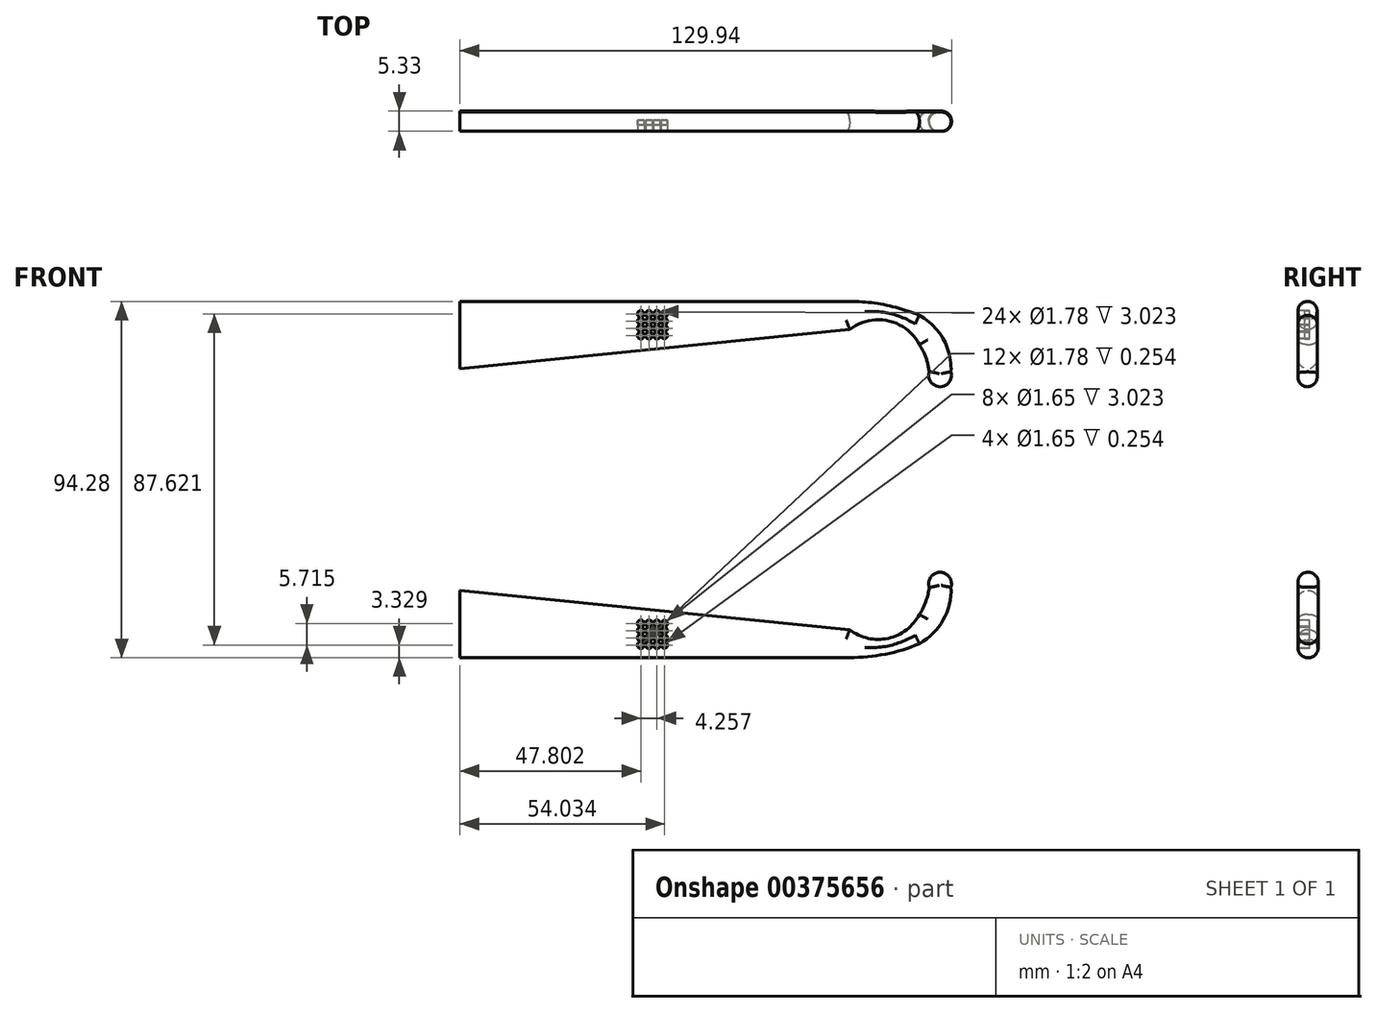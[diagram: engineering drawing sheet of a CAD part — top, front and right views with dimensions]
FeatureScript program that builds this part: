
annotation { "Feature Type Name" : "Feature", "Feature Type Description" : "" }
export const myFeature = defineFeature(function(context is Context, id is Id, definition is map)
    precondition{}
    {
        {
            var Q0;
            Q0=qCreatedBy(makeId("Front.planeOp"),FACE);
            var sketch = newSketch(context, id + "F0", { "sketchPlane" : qUnion([Q0])});
            skLineSegment(sketch, "E0", {"start": v(-73.1, 47.14) * mm, "end": v(-73.1, 29.36) * mm});
            skLineSegment(sketch, "E1", {"start": v(-73.1, 47.14) * mm, "end": v(29.93, 47.14) * mm});
            skLineSegment(sketch, "E2", {"start": v(-73.1, 29.36) * mm, "end": v(29.93, 39.72) * mm});
            skArc(sketch, "E3", {"start": v(48.35, 43.46) * mm, "mid": v(39.32, 46.2) * mm, "end": v(29.93, 47.14) * mm});
            skArc(sketch, "E4", {"start": v(56.7, 28.5) * mm, "mid": v(54.65, 37.16) * mm, "end": v(48.35, 43.46) * mm});
            skArc(sketch, "E5", {"start": v(48.35, 35.69) * mm, "mid": v(40.09, 42.02) * mm, "end": v(29.93, 39.72) * mm});
            skArc(sketch, "E6", {"start": v(50.94, 28.5) * mm, "mid": v(50.07, 32.24) * mm, "end": v(48.35, 35.69) * mm});
            skArc(sketch, "E7", {"start": v(50.94, 28.5) * mm, "mid": v(53.82, 24.55) * mm, "end": v(56.7, 28.5) * mm});
            skLineSegment(sketch, "E8", {"start": v(-76.71, 0) * mm, "end": v(75.51, 0) * mm});
            skLineSegment(sketch, "E9.MirrorCS", {"start": v(-73.1, -29.36) * mm, "end": v(29.93, -39.72) * mm});
            skLineSegment(sketch, "E10.MirrorCS", {"start": v(-73.1, -47.14) * mm, "end": v(29.93, -47.14) * mm});
            skLineSegment(sketch, "E11.MirrorCS", {"start": v(-73.1, -47.14) * mm, "end": v(-73.1, -29.36) * mm});
            skArc(sketch, "E12.MirrorCS", {"start": v(48.35, -43.46) * mm, "mid": v(39.32, -46.2) * mm, "end": v(29.93, -47.14) * mm});
            skArc(sketch, "E13.MirrorCS", {"start": v(56.7, -28.5) * mm, "mid": v(54.65, -37.16) * mm, "end": v(48.35, -43.46) * mm});
            skArc(sketch, "E14.MirrorCS", {"start": v(50.94, -28.5) * mm, "mid": v(53.82, -24.55) * mm, "end": v(56.7, -28.5) * mm});
            skArc(sketch, "E15.MirrorCS", {"start": v(50.94, -28.5) * mm, "mid": v(50.07, -32.24) * mm, "end": v(48.35, -35.69) * mm});
            skArc(sketch, "E16.MirrorCS", {"start": v(48.35, -35.69) * mm, "mid": v(40.09, -42.02) * mm, "end": v(29.93, -39.72) * mm});
            skSolve(sketch);
        }
        {
            var Q0;
            Q0 = qSketchRegion(id + "F0", true);
            extrude(context, id + "F1", {"entities" : qUnion([Q0]), "depth" : 5.08 * mm});
        }
        {
            var Q0;
            Q0=makeQuery(id+"F1.opExtrude","CAP_EDGE",EDGE,{"disambiguationData":[OSD([sQuery(id+"F0.wireOp",EDGE,"E3")])],"isStart":false});
            var Q1;
            Q1=makeQuery(id+"F1.opExtrude","CAP_EDGE",EDGE,{"disambiguationData":[OSD([sQuery(id+"F0.wireOp",EDGE,"E3")])],"isStart":true});
            var Q2;
            Q2=makeQuery(id+"F1.opExtrude","CAP_EDGE",EDGE,{"disambiguationData":[OSD([sQuery(id+"F0.wireOp",EDGE,"E4")])],"isStart":false});
            var Q3;
            Q3=makeQuery(id+"F1.opExtrude","CAP_EDGE",EDGE,{"disambiguationData":[OSD([sQuery(id+"F0.wireOp",EDGE,"E6")])],"isStart":false});
            var Q4;
            Q4=makeQuery(id+"F1.opExtrude","CAP_EDGE",EDGE,{"disambiguationData":[OSD([sQuery(id+"F0.wireOp",EDGE,"E5")])],"isStart":false});
            var Q5;
            Q5=makeQuery(id+"F1.opExtrude","CAP_EDGE",EDGE,{"disambiguationData":[OSD([sQuery(id+"F0.wireOp",EDGE,"E7")])],"isStart":false});
            var Q6;
            Q6=makeQuery(id+"F1.opExtrude","CAP_EDGE",EDGE,{"disambiguationData":[OSD([sQuery(id+"F0.wireOp",EDGE,"E7")])],"isStart":true});
            var Q7;
            Q7=makeQuery(id+"F1.opExtrude","CAP_EDGE",EDGE,{"disambiguationData":[OSD([sQuery(id+"F0.wireOp",EDGE,"E4")])],"isStart":true});
            var Q8;
            Q8=makeQuery(id+"F1.opExtrude","CAP_EDGE",EDGE,{"disambiguationData":[OSD([sQuery(id+"F0.wireOp",EDGE,"E6")])],"isStart":true});
            var Q9;
            Q9=makeQuery(id+"F1.opExtrude","CAP_EDGE",EDGE,{"disambiguationData":[OSD([sQuery(id+"F0.wireOp",EDGE,"E5")])],"isStart":true});
            var Q10;
            Q10=makeQuery(id+"F1.opExtrude","CAP_EDGE",EDGE,{"disambiguationData":[OSD([sQuery(id+"F0.wireOp",EDGE,"E2")])],"isStart":false});
            var Q11;
            Q11=makeQuery(id+"F1.opExtrude","CAP_EDGE",EDGE,{"disambiguationData":[OSD([sQuery(id+"F0.wireOp",EDGE,"E2")])],"isStart":true});
            fillet(context, id + "F2", {"entities" : qUnion([Q0, Q1, Q2, Q3, Q4, Q5, Q6, Q7, Q8, Q9, Q10, Q11]), "radius" : 2.54 * mm, "tangentPropagation" : true, "allowEdgeOverflow" : false});
        }
        {
            var Q0;
            Q0=makeQuery(id+"F2.opFillet","SPLIT",FACE,{"disambiguationData":[OD(0.0)],"derivedFrom":makeQuery(id+"F1.opExtrude","CAP_FACE",FACE,{"disambiguationData":[OSD([sQuery(id+"F0.wireOp",EDGE,"E0"),sQuery(id+"F0.wireOp",EDGE,"E1"),sQuery(id+"F0.wireOp",EDGE,"E2"),sQuery(id+"F0.wireOp",EDGE,"E3"),sQuery(id+"F0.wireOp",EDGE,"E4"),sQuery(id+"F0.wireOp",EDGE,"E5"),sQuery(id+"F0.wireOp",EDGE,"E6"),sQuery(id+"F0.wireOp",EDGE,"E7")])],"isStart":false})});
            var sketch = newSketch(context, id + "F3", { "sketchPlane" : qUnion([Q0])});
            skCircle(sketch, "E17", {"center": v(-21.04, 43.81) * mm, "radius": 0.89 * mm});
            skCircle(sketch, "E18", {"center": v(-21.05, 41.9) * mm, "radius": 0.89 * mm});
            skCircle(sketch, "E19", {"center": v(-21.05, 40) * mm, "radius": 0.89 * mm});
            skCircle(sketch, "E20", {"center": v(-21.05, 38.1) * mm, "radius": 0.89 * mm});
            skCircle(sketch, "E21", {"center": v(-19.07, 43.81) * mm, "radius": 0.83 * mm});
            skCircle(sketch, "E22", {"center": v(-19.07, 41.89) * mm, "radius": 0.83 * mm});
            skCircle(sketch, "E23", {"center": v(-19.07, 40) * mm, "radius": 0.83 * mm});
            skCircle(sketch, "E24", {"center": v(-19.07, 38.1) * mm, "radius": 0.83 * mm});
            skCircle(sketch, "E25", {"center": v(-23.16, 43.81) * mm, "radius": 0.89 * mm});
            skCircle(sketch, "E26", {"center": v(-23.16, 41.89) * mm, "radius": 0.89 * mm});
            skCircle(sketch, "E27", {"center": v(-23.16, 40) * mm, "radius": 0.89 * mm});
            skCircle(sketch, "E28", {"center": v(-23.16, 38.1) * mm, "radius": 0.89 * mm});
            skCircle(sketch, "E29", {"center": v(-25.3, 43.81) * mm, "radius": 0.89 * mm});
            skCircle(sketch, "E30", {"center": v(-25.3, 41.89) * mm, "radius": 0.89 * mm});
            skCircle(sketch, "E31", {"center": v(-25.3, 40) * mm, "radius": 0.89 * mm});
            skCircle(sketch, "E32", {"center": v(-25.3, 38.1) * mm, "radius": 0.89 * mm});
            skCircle(sketch, "E33.MirrorC", {"center": v(-19.07, -43.81) * mm, "radius": 0.83 * mm});
            skCircle(sketch, "E34.MirrorC", {"center": v(-21.04, -43.81) * mm, "radius": 0.89 * mm});
            skCircle(sketch, "E35.MirrorC", {"center": v(-23.16, -43.81) * mm, "radius": 0.89 * mm});
            skCircle(sketch, "E36.MirrorC", {"center": v(-25.3, -43.81) * mm, "radius": 0.89 * mm});
            skCircle(sketch, "E37.MirrorC", {"center": v(-19.07, -41.89) * mm, "radius": 0.83 * mm});
            skCircle(sketch, "E38.MirrorC", {"center": v(-21.05, -41.9) * mm, "radius": 0.89 * mm});
            skCircle(sketch, "E39.MirrorC", {"center": v(-23.16, -41.89) * mm, "radius": 0.89 * mm});
            skCircle(sketch, "E40.MirrorC", {"center": v(-25.3, -41.89) * mm, "radius": 0.89 * mm});
            skCircle(sketch, "E41.MirrorC", {"center": v(-19.07, -40) * mm, "radius": 0.83 * mm});
            skCircle(sketch, "E42.MirrorC", {"center": v(-21.05, -40) * mm, "radius": 0.89 * mm});
            skCircle(sketch, "E43.MirrorC", {"center": v(-23.16, -40) * mm, "radius": 0.89 * mm});
            skCircle(sketch, "E44.MirrorC", {"center": v(-25.3, -40) * mm, "radius": 0.89 * mm});
            skCircle(sketch, "E45.MirrorC", {"center": v(-19.07, -38.1) * mm, "radius": 0.83 * mm});
            skCircle(sketch, "E46.MirrorC", {"center": v(-21.05, -38.1) * mm, "radius": 0.89 * mm});
            skCircle(sketch, "E47.MirrorC", {"center": v(-23.16, -38.1) * mm, "radius": 0.89 * mm});
            skCircle(sketch, "E48.MirrorC", {"center": v(-25.3, -38.1) * mm, "radius": 0.89 * mm});
            skSolve(sketch);
        }
        {
            var Q0;
            Q0 = qSketchRegion(id + "F3", true);
            extrude(context, id + "F4", {"entities" : qUnion([Q0]), "operationType" : NewBodyOperationType.REMOVE, "oppositeDirection" : true, "depth" : 3.02 * mm});
        }
        {
            var Q0;
            Q0=makeQuery(id+"F4.boolean.opBoolean","COPY",FACE,{"derivedFrom":makeQuery(id+"F4.opExtrude","CAP_FACE",FACE,{"disambiguationData":[OSD([sQuery(id+"F3.wireOp",EDGE,"E32")])],"isStart":false})});
            var Q1;
            Q1=makeQuery(id+"F4.boolean.opBoolean","COPY",FACE,{"derivedFrom":makeQuery(id+"F4.opExtrude","CAP_FACE",FACE,{"disambiguationData":[OSD([sQuery(id+"F3.wireOp",EDGE,"E28")])],"isStart":false})});
            var Q2;
            Q2=makeQuery(id+"F4.boolean.opBoolean","COPY",FACE,{"derivedFrom":makeQuery(id+"F4.opExtrude","CAP_FACE",FACE,{"disambiguationData":[OSD([sQuery(id+"F3.wireOp",EDGE,"E20")])],"isStart":false})});
            var Q3;
            Q3=makeQuery(id+"F4.boolean.opBoolean","COPY",FACE,{"derivedFrom":makeQuery(id+"F4.opExtrude","CAP_FACE",FACE,{"disambiguationData":[OSD([sQuery(id+"F3.wireOp",EDGE,"E24")])],"isStart":false})});
            var Q4;
            Q4=makeQuery(id+"F4.boolean.opBoolean","COPY",FACE,{"derivedFrom":makeQuery(id+"F4.opExtrude","CAP_FACE",FACE,{"disambiguationData":[OSD([sQuery(id+"F3.wireOp",EDGE,"E19")])],"isStart":false})});
            var Q5;
            Q5=makeQuery(id+"F4.boolean.opBoolean","COPY",FACE,{"derivedFrom":makeQuery(id+"F4.opExtrude","CAP_FACE",FACE,{"disambiguationData":[OSD([sQuery(id+"F3.wireOp",EDGE,"E27")])],"isStart":false})});
            var Q6;
            Q6=makeQuery(id+"F4.boolean.opBoolean","COPY",FACE,{"derivedFrom":makeQuery(id+"F4.opExtrude","CAP_FACE",FACE,{"disambiguationData":[OSD([sQuery(id+"F3.wireOp",EDGE,"E31")])],"isStart":false})});
            var Q7;
            Q7=makeQuery(id+"F4.boolean.opBoolean","COPY",FACE,{"derivedFrom":makeQuery(id+"F4.opExtrude","CAP_FACE",FACE,{"disambiguationData":[OSD([sQuery(id+"F3.wireOp",EDGE,"E23")])],"isStart":false})});
            var Q8;
            Q8=makeQuery(id+"F4.boolean.opBoolean","COPY",FACE,{"derivedFrom":makeQuery(id+"F4.opExtrude","CAP_FACE",FACE,{"disambiguationData":[OSD([sQuery(id+"F3.wireOp",EDGE,"E22")])],"isStart":false})});
            var Q9;
            Q9=makeQuery(id+"F4.boolean.opBoolean","COPY",FACE,{"derivedFrom":makeQuery(id+"F4.opExtrude","CAP_FACE",FACE,{"disambiguationData":[OSD([sQuery(id+"F3.wireOp",EDGE,"E18")])],"isStart":false})});
            var Q10;
            Q10=makeQuery(id+"F4.boolean.opBoolean","COPY",FACE,{"derivedFrom":makeQuery(id+"F4.opExtrude","CAP_FACE",FACE,{"disambiguationData":[OSD([sQuery(id+"F3.wireOp",EDGE,"E26")])],"isStart":false})});
            var Q11;
            Q11=makeQuery(id+"F4.boolean.opBoolean","COPY",FACE,{"derivedFrom":makeQuery(id+"F4.opExtrude","CAP_FACE",FACE,{"disambiguationData":[OSD([sQuery(id+"F3.wireOp",EDGE,"E30")])],"isStart":false})});
            var Q12;
            Q12=makeQuery(id+"F4.boolean.opBoolean","COPY",FACE,{"derivedFrom":makeQuery(id+"F4.opExtrude","CAP_FACE",FACE,{"disambiguationData":[OSD([sQuery(id+"F3.wireOp",EDGE,"E21")])],"isStart":false})});
            var Q13;
            Q13=makeQuery(id+"F4.boolean.opBoolean","COPY",FACE,{"derivedFrom":makeQuery(id+"F4.opExtrude","CAP_FACE",FACE,{"disambiguationData":[OSD([sQuery(id+"F3.wireOp",EDGE,"E17")])],"isStart":false})});
            var Q14;
            Q14=makeQuery(id+"F4.boolean.opBoolean","COPY",FACE,{"derivedFrom":makeQuery(id+"F4.opExtrude","CAP_FACE",FACE,{"disambiguationData":[OSD([sQuery(id+"F3.wireOp",EDGE,"E25")])],"isStart":false})});
            var Q15;
            Q15=makeQuery(id+"F4.boolean.opBoolean","COPY",FACE,{"derivedFrom":makeQuery(id+"F4.opExtrude","CAP_FACE",FACE,{"disambiguationData":[OSD([sQuery(id+"F3.wireOp",EDGE,"E29")])],"isStart":false})});
            extrude(context, id + "F5", {"entities" : qUnion([Q0, Q1, Q2, Q3, Q4, Q5, Q6, Q7, Q8, Q9, Q10, Q11, Q12, Q13, Q14, Q15]), "depth" : 1.27 * mm});
        }
        {
            var Q0;
            Q0=makeQuery(id+"F1.opExtrude","CAP_FACE",FACE,{"disambiguationData":[OSD([sQuery(id+"F0.wireOp",EDGE,"E9.MirrorCS"),sQuery(id+"F0.wireOp",EDGE,"E10.MirrorCS"),sQuery(id+"F0.wireOp",EDGE,"E11.MirrorCS"),sQuery(id+"F0.wireOp",EDGE,"E12.MirrorCS"),sQuery(id+"F0.wireOp",EDGE,"E13.MirrorCS"),sQuery(id+"F0.wireOp",EDGE,"E14.MirrorCS"),sQuery(id+"F0.wireOp",EDGE,"E15.MirrorCS"),sQuery(id+"F0.wireOp",EDGE,"E16.MirrorCS")])],"isStart":false});
            extrude(context, id + "F6", {"entities" : qUnion([Q0]), "operationType" : NewBodyOperationType.ADD, "oppositeDirection" : true, "depth" : 5.33 * mm});
        }
        {
            var Q0;
            Q0=makeQuery(id+"F1.opExtrude","CAP_EDGE",EDGE,{"disambiguationData":[OSD([sQuery(id+"F0.wireOp",EDGE,"E9.MirrorCS")])],"isStart":false});
            var Q1;
            Q1=makeQuery(id+"F1.opExtrude","CAP_EDGE",EDGE,{"disambiguationData":[OSD([sQuery(id+"F0.wireOp",EDGE,"E10.MirrorCS")])],"isStart":false});
            var Q2;
            Q2=makeQuery(id+"F1.opExtrude","CAP_EDGE",EDGE,{"disambiguationData":[OSD([sQuery(id+"F0.wireOp",EDGE,"E16.MirrorCS")])],"isStart":false});
            var Q3;
            Q3=makeQuery(id+"F1.opExtrude","CAP_EDGE",EDGE,{"disambiguationData":[OSD([sQuery(id+"F0.wireOp",EDGE,"E14.MirrorCS")])],"isStart":false});
            var Q4;
            Q4=makeQuery(id+"F1.opExtrude","CAP_EDGE",EDGE,{"disambiguationData":[OSD([sQuery(id+"F0.wireOp",EDGE,"E13.MirrorCS")])],"isStart":false});
            var Q5;
            Q5=makeQuery(id+"F1.opExtrude","CAP_EDGE",EDGE,{"disambiguationData":[OSD([sQuery(id+"F0.wireOp",EDGE,"E12.MirrorCS")])],"isStart":false});
            var Q6;
            Q6=makeQuery(id+"F1.opExtrude","CAP_EDGE",EDGE,{"disambiguationData":[OSD([sQuery(id+"F0.wireOp",EDGE,"E15.MirrorCS")])],"isStart":false});
            var Q7;
            Q7=makeQuery(id+"F6.opExtrude","CAP_EDGE",EDGE,{"disambiguationData":[OSD([sQuery(id+"F0.wireOp",EDGE,"E14.MirrorCS")])],"isStart":false});
            var Q8;
            Q8=makeQuery(id+"F6.opExtrude","CAP_EDGE",EDGE,{"disambiguationData":[OSD([sQuery(id+"F0.wireOp",EDGE,"E13.MirrorCS")])],"isStart":false});
            var Q9;
            Q9=makeQuery(id+"F6.opExtrude","CAP_EDGE",EDGE,{"disambiguationData":[OSD([sQuery(id+"F0.wireOp",EDGE,"E15.MirrorCS")])],"isStart":false});
            var Q10;
            Q10=makeQuery(id+"F6.opExtrude","CAP_EDGE",EDGE,{"disambiguationData":[OSD([sQuery(id+"F0.wireOp",EDGE,"E12.MirrorCS")])],"isStart":false});
            var Q11;
            Q11=makeQuery(id+"F6.opExtrude","CAP_EDGE",EDGE,{"disambiguationData":[OSD([sQuery(id+"F0.wireOp",EDGE,"E16.MirrorCS")])],"isStart":false});
            var Q12;
            Q12=makeQuery(id+"F6.opExtrude","CAP_EDGE",EDGE,{"disambiguationData":[OSD([sQuery(id+"F0.wireOp",EDGE,"E9.MirrorCS")])],"isStart":false});
            fillet(context, id + "F7", {"entities" : qUnion([Q0, Q1, Q2, Q3, Q4, Q5, Q6, Q7, Q8, Q9, Q10, Q11, Q12]), "radius" : 2.54 * mm, "tangentPropagation" : true, "allowEdgeOverflow" : false});
        }
    });
